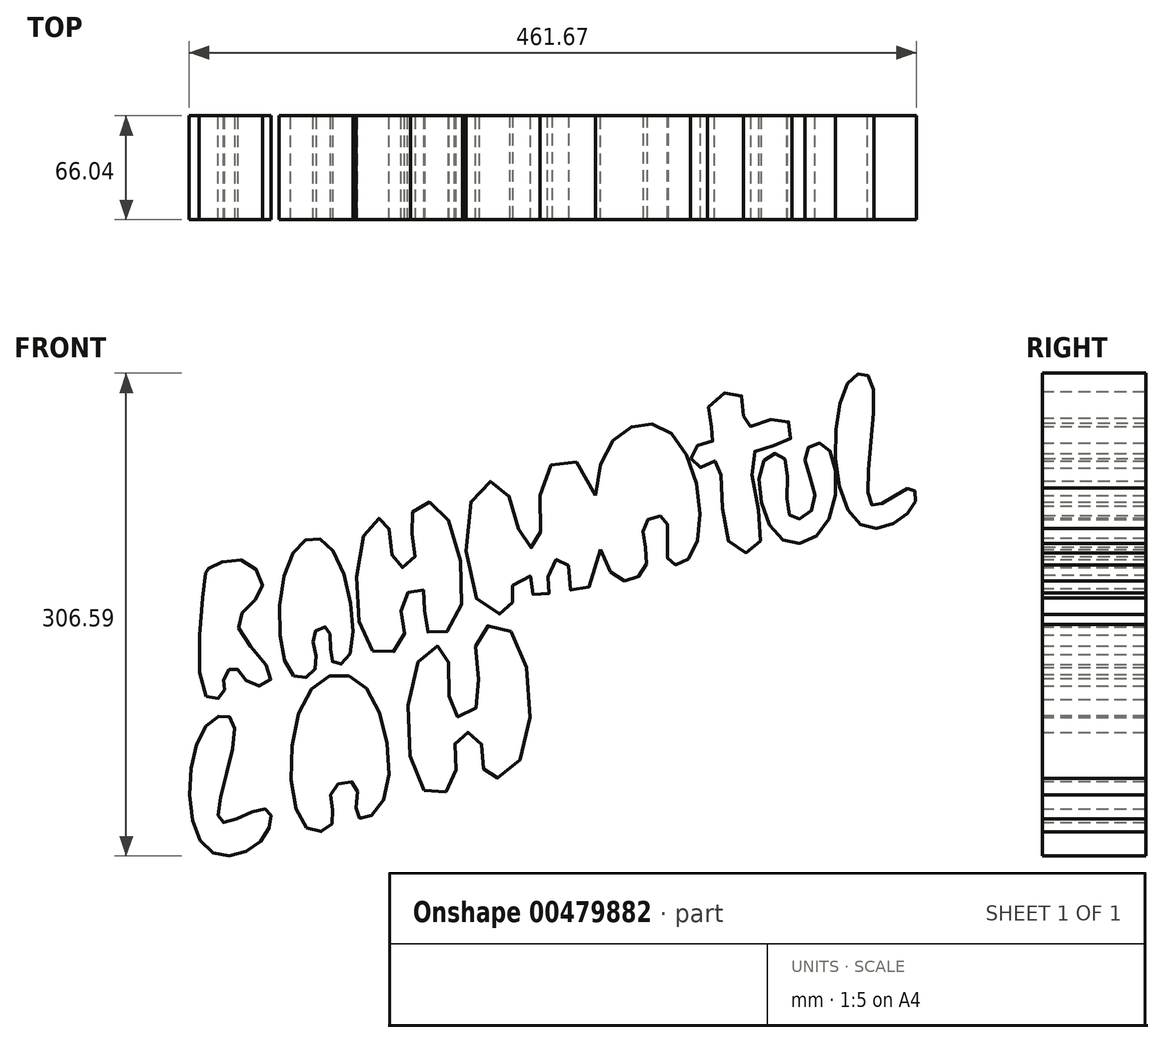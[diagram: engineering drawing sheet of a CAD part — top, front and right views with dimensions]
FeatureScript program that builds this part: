
annotation { "Feature Type Name" : "Feature", "Feature Type Description" : "" }
export const myFeature = defineFeature(function(context is Context, id is Id, definition is map)
    precondition{}
    {
        {
            var Q0;
            Q0=qCreatedBy(makeId("Front.planeOp"),FACE);
            var sketch = newSketch(context, id + "F0", { "sketchPlane" : qUnion([Q0])});
            skFitSpline(sketch, "E0", {"points": [v(-225.44, -67.67) * mm, v(-225.44, 12.51) * mm, v(-225.01, 13.07) * mm, v(-203.9, 19.16) * mm, v(-190.1, 0) * mm, v(-205.18, -21.73) * mm, v(-184.06, -55.29) * mm, v(-196.56, -60.2) * mm, v(-207.77, -49.2) * mm, v(-214.24, -57.1) * mm, v(-214.24, -65.72) * mm, v(-225.44, -67.67) * mm]});
            skFitSpline(sketch, "E1", {"points": [v(-169.84, -54.63) * mm, v(-171.56, 21.17) * mm, v(-148.28, 29.18) * mm, v(-135.35, -43.38) * mm, v(-145.27, -45.38) * mm, v(-147.85, -24.58) * mm, v(-156.9, -27.62) * mm, v(-155.61, -49.2) * mm, v(-169.84, -54.63) * mm]});
            skFitSpline(sketch, "E2", {"points": [v(-119.83, -38.9) * mm, v(-123.28, 38.55) * mm, v(-110.78, 43.46) * mm, v(-104.75, 15.45) * mm, v(-93.1, 19.68) * mm, v(-95.26, 47.07) * mm, v(-78.88, 53.96) * mm, v(-67.25, -21.14) * mm, v(-85.78, -25.2) * mm, v(-87.5, 0) * mm, v(-100.87, -6.27) * mm, v(-100, -31.89) * mm, v(-119.83, -38.9) * mm]});
            skFitSpline(sketch, "E3", {"points": [v(-161.65, 0) * mm, v(-148.28, 6.14) * mm, v(-143.54, -7.81) * mm, v(-157.77, -14.94) * mm, v(-161.65, 0) * mm]});
            skFitSpline(sketch, "E4", {"points": [v(-47.85, -13.38) * mm, v(-54.31, 62.34) * mm, v(-36.2, 64.98) * mm, v(-22.85, 29.18) * mm, v(-14.66, 29.18) * mm, v(-10.78, 73.19) * mm, v(11.64, 79.66) * mm, v(20.26, 5.42) * mm, v(6.03, 0) * mm, v(3.02, 20.27) * mm, v(-8.62, 12.6) * mm, v(-6.03, 0) * mm, v(-16.81, -4.42) * mm, v(-19.4, 8.63) * mm, v(-32.33, 0) * mm, v(-31.04, -10.25) * mm, v(-47.85, -13.38) * mm]});
            skFitSpline(sketch, "E5", {"points": [v(35.78, 7.31) * mm, v(28.88, 88.51) * mm, v(69.83, 99.47) * mm, v(83.63, 23.28) * mm, v(68.54, 18.06) * mm, v(66.38, 45.03) * mm, v(53.02, 42.03) * mm, v(53.88, 15.12) * mm, v(35.78, 7.31) * mm]});
            skFitSpline(sketch, "E6", {"points": [v(53.02, 64.56) * mm, v(67.68, 66.52) * mm, v(67.25, 53.96) * mm, v(46.55, 49.65) * mm, v(53.02, 64.56) * mm]});
            skFitSpline(sketch, "E7", {"points": [v(93.54, 116.23) * mm, v(96.99, 95.24) * mm, v(83.63, 89.66) * mm, v(86.64, 77.6) * mm, v(99.14, 81.64) * mm, v(107.33, 29.18) * mm, v(125.87, 29.18) * mm, v(122.42, 87.07) * mm, v(144.84, 94.83) * mm, v(141.39, 108.92) * mm, v(117.68, 104.23) * mm, v(113.8, 124.24) * mm, v(93.54, 116.23) * mm]});
            skFitSpline(sketch, "E8", {"points": [v(128.89, 82.04) * mm, v(138.8, 33.17) * mm, v(168.54, 42.03) * mm, v(167.68, 91.94) * mm, v(155.18, 87.07) * mm, v(160.79, 53.96) * mm, v(146.13, 46.06) * mm, v(141.82, 83.61) * mm, v(128.89, 82.04) * mm]});
            skFitSpline(sketch, "E9", {"points": [v(181.9, 130.97) * mm, v(189.24, 42.03) * mm, v(224.15, 53.96) * mm, v(221.56, 64.56) * mm, v(197.43, 53.96) * mm, v(197, 133.17) * mm, v(181.9, 130.97) * mm]});
            skFitSpline(sketch, "E10", {"points": [v(228.03, 87.07) * mm, v(254.76, 94.66) * mm, v(259.5, 87.07) * mm, v(229.75, 74.08) * mm, v(228.03, 87.07) * mm]});
            skFitSpline(sketch, "E11", {"points": [v(-225.44, -86.38) * mm, v(-225.44, -164.04) * mm, v(-188.37, -156.97) * mm, v(-187.94, -139.17) * mm, v(-216.4, -146.95) * mm, v(-207.77, -84.56) * mm, v(-225.44, -86.38) * mm]});
            skFitSpline(sketch, "E12", {"points": [v(-161.65, -151.1) * mm, v(-161.65, -67.67) * mm, v(-126.73, -59.43) * mm, v(-113.8, -135.87) * mm, v(-129.32, -143.8) * mm, v(-130.61, -123.49) * mm, v(-145.27, -126.85) * mm, v(-145.27, -147.98) * mm, v(-161.65, -151.1) * mm]});
            skFitSpline(sketch, "E13", {"points": [v(-144.84, -93.54) * mm, v(-131.04, -89.56) * mm, v(-128.02, -105.93) * mm, v(-148.28, -111.54) * mm, v(-144.84, -93.54) * mm]});
            skFitSpline(sketch, "E14", {"points": [v(-87.07, -127.3) * mm, v(-89.23, -43) * mm, v(-73.28, -38.9) * mm, v(-68.54, -78.84) * mm, v(-53.45, -74.05) * mm, v(-53.02, -29.96) * mm, v(-33.2, -25.1) * mm, v(-26.73, -109.01) * mm, v(-47.85, -117.4) * mm, v(-52.16, -93.54) * mm, v(-65.95, -93.54) * mm, v(-68.1, -122.25) * mm, v(-87.07, -127.3) * mm]});
            skSolve(sketch);
        }
        {
            var Q0;
            Q0=makeQuery(id+"F0.imprint","IMPRINT",FACE,{"disambiguationData":[TD([[makeQuery(id+"F0.imprint","IMPRINT",EDGE,{"derivedFrom":sQuery(id+"F0.wireOp",EDGE,"E14")}),-1.0]])]});
            var Q1;
            Q1=makeQuery(id+"F0.imprint","IMPRINT",FACE,{"disambiguationData":[TD([[makeQuery(id+"F0.imprint","IMPRINT",EDGE,{"derivedFrom":sQuery(id+"F0.wireOp",EDGE,"E11")}),1.0]])]});
            var Q2;
            Q2=makeQuery(id+"F0.imprint","IMPRINT",FACE,{"disambiguationData":[TD([[makeQuery(id+"F0.imprint","IMPRINT",EDGE,{"derivedFrom":sQuery(id+"F0.wireOp",EDGE,"E1")}),-1.0]])]});
            var Q3;
            Q3=makeQuery(id+"F0.imprint","IMPRINT",FACE,{"disambiguationData":[TD([[makeQuery(id+"F0.imprint","IMPRINT",EDGE,{"derivedFrom":sQuery(id+"F0.wireOp",EDGE,"E3")}),-1.0]])]});
            var Q4;
            Q4=makeQuery(id+"F0.imprint","IMPRINT",FACE,{"disambiguationData":[TD([[makeQuery(id+"F0.imprint","IMPRINT",EDGE,{"derivedFrom":sQuery(id+"F0.wireOp",EDGE,"E2")}),-1.0]])]});
            var Q5;
            Q5=makeQuery(id+"F0.imprint","IMPRINT",FACE,{"disambiguationData":[TD([[makeQuery(id+"F0.imprint","IMPRINT",EDGE,{"derivedFrom":sQuery(id+"F0.wireOp",EDGE,"E0")}),-1.0]])]});
            var Q6;
            {var subQ0=sQuery(id+"F0.wireOp",EDGE,"E5");var subQ1=sQuery(id+"F0.wireOp",EDGE,"E4");var subQ2=makeQuery(id+"F0.imprint","INTERSECT",VERTEX,{"disambiguationData":[OD(0.0)],"derivedFrom":[subQ1,subQ0]});Q6=makeQuery(id+"F0.imprint","IMPRINT",FACE,{"disambiguationData":[TD([[makeQuery(id+"F0.imprint","IMPRINT",EDGE,{"disambiguationData":[TD([[subQ2,-1.0]])],"derivedFrom":subQ1}),-1.0]])]});}
            var Q7;
            Q7=makeQuery(id+"F0.imprint","IMPRINT",FACE,{"disambiguationData":[TD([[makeQuery(id+"F0.imprint","IMPRINT",EDGE,{"derivedFrom":sQuery(id+"F0.wireOp",EDGE,"E6")}),-1.0]])]});
            var Q8;
            Q8=makeQuery(id+"F0.imprint","IMPRINT",FACE,{"disambiguationData":[TD([[makeQuery(id+"F0.imprint","IMPRINT",EDGE,{"derivedFrom":sQuery(id+"F0.wireOp",EDGE,"E13")}),-1.0]])]});
            var Q9;
            Q9=makeQuery(id+"F0.imprint","IMPRINT",FACE,{"disambiguationData":[TD([[makeQuery(id+"F0.imprint","IMPRINT",EDGE,{"derivedFrom":sQuery(id+"F0.wireOp",EDGE,"E12")}),-1.0]])]});
            var Q10;
            Q10=makeQuery(id+"F0.imprint","IMPRINT",FACE,{"disambiguationData":[TD([[makeQuery(id+"F0.imprint","IMPRINT",EDGE,{"derivedFrom":sQuery(id+"F0.wireOp",EDGE,"E6")}),1.0]])]});
            var Q11;
            {var subQ0=sQuery(id+"F0.wireOp",EDGE,"E5");var subQ1=sQuery(id+"F0.wireOp",EDGE,"E4");var subQ2=makeQuery(id+"F0.imprint","INTERSECT",VERTEX,{"disambiguationData":[OD(0.0)],"derivedFrom":[subQ1,subQ0]});Q11=makeQuery(id+"F0.imprint","IMPRINT",FACE,{"disambiguationData":[TD([[makeQuery(id+"F0.imprint","IMPRINT",EDGE,{"disambiguationData":[TD([[subQ2,1.0]])],"derivedFrom":subQ1}),-1.0]])]});}
            var Q12;
            Q12=makeQuery(id+"F0.imprint","IMPRINT",FACE,{"disambiguationData":[TD([[makeQuery(id+"F0.imprint","IMPRINT",EDGE,{"derivedFrom":sQuery(id+"F0.wireOp",EDGE,"E9")}),1.0]])]});
            var Q13;
            Q13=makeQuery(id+"F0.imprint","IMPRINT",FACE,{"disambiguationData":[TD([[makeQuery(id+"F0.imprint","IMPRINT",EDGE,{"derivedFrom":sQuery(id+"F0.wireOp",EDGE,"E8")}),1.0]])]});
            var Q14;
            Q14=makeQuery(id+"F0.imprint","IMPRINT",FACE,{"disambiguationData":[TD([[makeQuery(id+"F0.imprint","IMPRINT",EDGE,{"derivedFrom":sQuery(id+"F0.wireOp",EDGE,"E7")}),1.0]])]});
            extrude(context, id + "F1", {"entities" : qUnion([Q0, Q1, Q2, Q3, Q4, Q5, Q6, Q7, Q8, Q9, Q10, Q11, Q12, Q13, Q14]), "depth" : 66.04 * mm});
        }
    });
